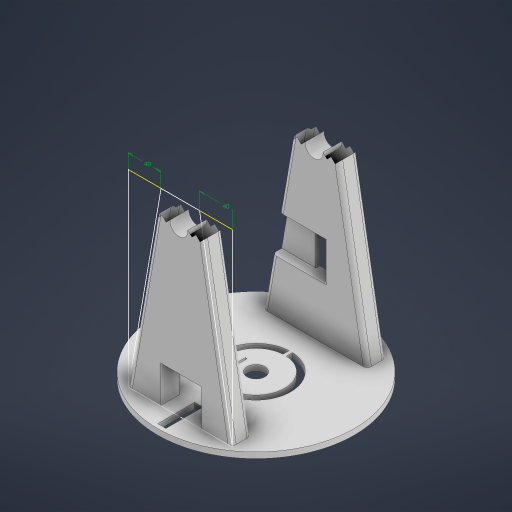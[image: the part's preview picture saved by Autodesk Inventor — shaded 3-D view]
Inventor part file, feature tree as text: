
AUTODESK INVENTOR PART (.ipt)
format: ipt  version: 2023 (Build 270158030, 158C)  size: 468,480 bytes
history: native  units: in
note: dims shown in document units (in); Inventor stores cm internally (conversion verified against a paired STEP export)
features: sketch x16, extrude x14, fillet x2, delete_face x2, split x1
ambient origin geometry x8: Origin, YZ Plane, XZ Plane, XY Plane, X Axis, Y Axis, Z Axis, Center Point
bodies: Solid1 (feature_tree)
feature tree (35):
  extrude  "Extrusion1"  Depth=0.2756in TaperAngle=0.0deg
  extrude  "Extrusion2"  Depth=0.2756in TaperAngle=0.0deg
  sketch  "Sketch4"  dims[d10=5.0in d11=0.9055in]
  sketch  "Sketch5"  dims[d12=0.1969in d13=5.0in d14=0.9055in]
  sketch  "Sketch6"  dims[d16=2.7953in d17=9.0551in d18=0.0in]
  extrude  "Extrusion4"  Depth=0.9055in
  extrude  "Extrusion5"  Depth=0.9055in
  extrude  "Extrusion6"  Depth=9.0551in TaperAngle=0.0deg
  extrude  "Extrusion7"  Depth=1.9685in
  sketch  "Sketch9"  dims[d28=1.5748in d29=1.5748in]
  sketch  "Sketch10"  dims[d30=1.5748in d31=1.5748in]
  extrude  "Extrusion8"  Depth=1.7717in
  fillet  "Fillet1"  Radius=9.0551in
  fillet  "Fillet2"  Radius=7.2835in
  extrude  "Extrusion9"  Depth=1.5748in
  extrude  "Extrusion10"  Depth=1.5748in
  sketch  "Sketch16"  dims[d37=10.9085in d38=0.0in d39=0.2756in d40=0.0in]
  extrude  "Extrusion13"  Depth=0.1969in
  extrude  "Extrusion14"  Depth=0.1969in
  extrude  "Extrusion16"  Depth=0.2756in TaperAngle=0.0deg
  extrude  "Extrusion17"  Depth=0.3937in
  extrude  "Extrusion18"  Depth=0.3937in TaperAngle=0.0deg
  split  "Split1"
  delete_face  "Delete Face1"
  delete_face  "Delete Face2"
  sketch  "Sketch1"  dims[d0=9.4488in d1=0.2756in d2=0.0in]
  sketch  "Sketch2"  dims[d3=0.8583in d4=0.2756in d5=0.0in]
  sketch  "Sketch7"  dims[d19=9.0551in d20=0.0in d21=1.9685in]
  sketch  "Sketch8"  dims[d22=1.7717in d23=0.8858in d24=9.0551in d25=0.0in d26=7.2835in d27=0.0in]
  sketch  "Sketch11"  dims[d32=10.9085in d33=0.0in d34=0.1969in]
  sketch  "Sketch12"  dims[d35=0.1969in d36=0.8583in]
  sketch  "Sketch20"  dims[d51=1.7717in d52=0.3937in]
  sketch  "Sketch21"  dims[d53=2.7559in d54=0.3937in d55=0.0in]
  sketch  "Sketch22"  dims[d57=2.9528in]
  sketch  "Sketch23"  dims[d58=1.9685in d59=0.9449in d60=0.5118in d61=1.5026in d62=0.6299in d63=0.0in d66=2.7559in d67=3.3465in d68=0.0787in d69=0.0787in d70=0.0787in d71=0.4469in d72=0.0in d73=0.3346in d74=0.3346in d75=0.0787in d76=0.4469in d77=0.0in d80=1.9685in d81=1.8898in d82=0.4469in d83=0.0in d84=0.2756in d85=45.0deg d86=0.2756in d87=135.0deg d88=0.2756in d89=135.0deg d90=0.2756in d91=135.0deg d92=0.0984in d93=135.0deg d94=0.0in]
